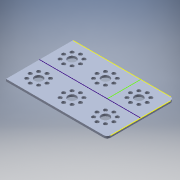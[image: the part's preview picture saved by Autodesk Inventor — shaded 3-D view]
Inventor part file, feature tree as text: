
AUTODESK INVENTOR PART (.ipt)
format: ipt  version: 2017 (Build 210142000, 142)  size: 330,752 bytes
history: native  units: in
note: dims shown in document units (in); Inventor stores cm internally (conversion verified against a paired STEP export)
features: other x2, sketch x2, fillet x1, split x1, imported_body x1, projected_geometry x1
ambient origin geometry x8: Origin, YZ Plane, XZ Plane, XY Plane, X Axis, Y Axis, Z Axis, Center Point
bodies: Body1 (feature_tree)
feature tree (8):
  other  "Flat Plate1"
  other  "Flat Plate"
  fillet  "Fillet1"  Radius=0.125in
  split  "Split1"
  sketch  "Sketch2"
  imported_body  "Base1"
  sketch  "Sketch1"  dims[d1=2.5in]
  projected_geometry  "Projected Loop1"
